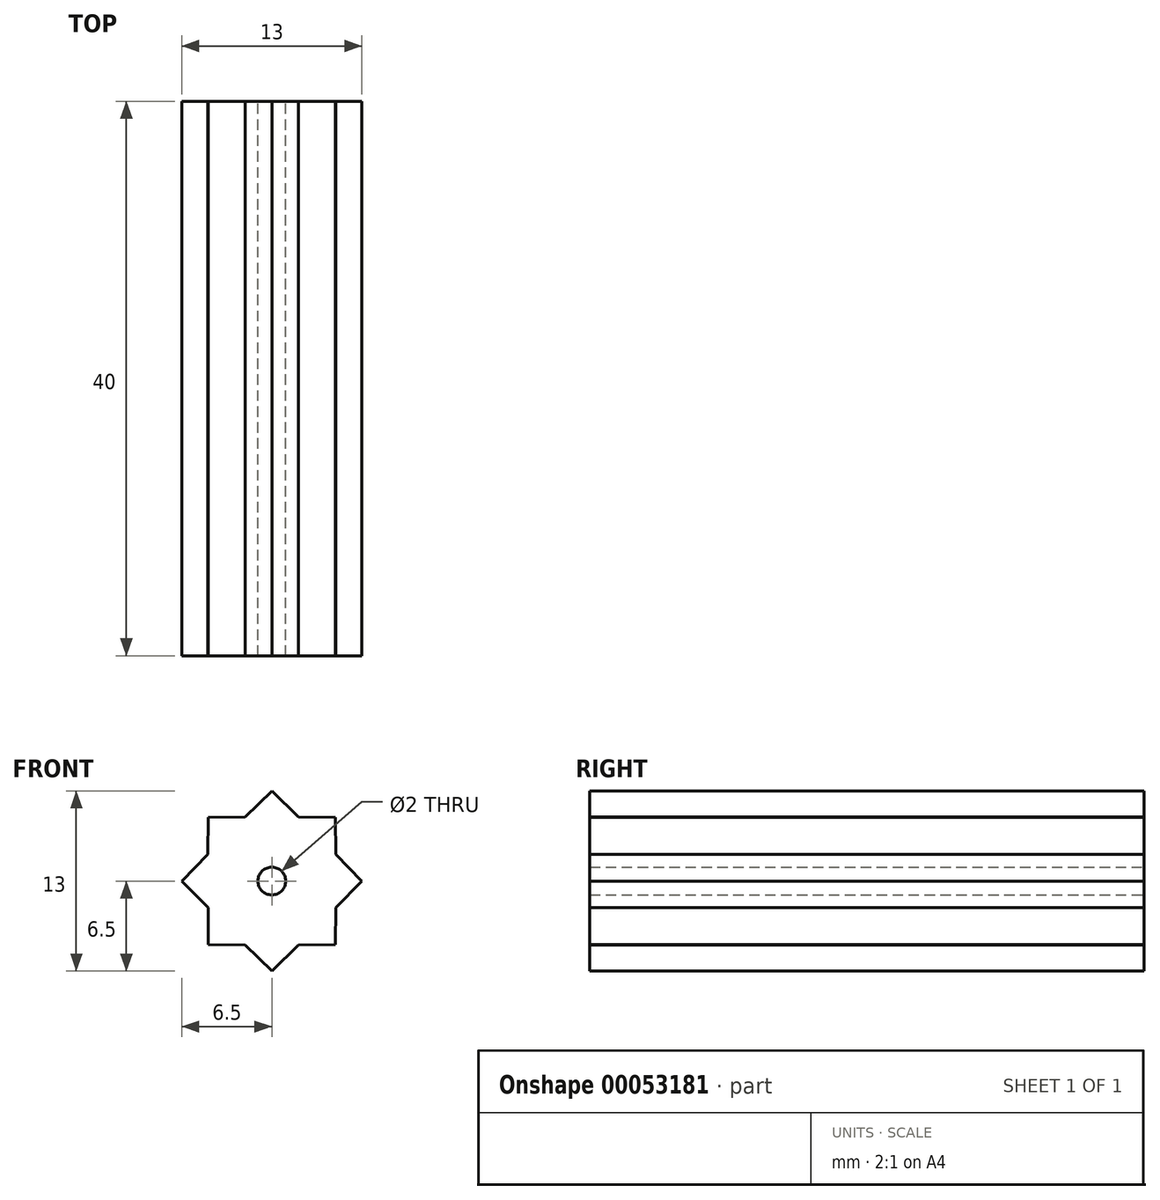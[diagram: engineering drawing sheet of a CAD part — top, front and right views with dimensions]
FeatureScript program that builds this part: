
annotation { "Feature Type Name" : "Feature", "Feature Type Description" : "" }
export const myFeature = defineFeature(function(context is Context, id is Id, definition is map)
    precondition{}
    {
        {
            var Q0;
            Q0=qCreatedBy(makeId("Front.planeOp"),FACE);
            var sketch = newSketch(context, id + "F0", { "sketchPlane" : qUnion([Q0])});
            skCircle(sketch, "E0", {"center": v(0, 0) * mm, "radius": 1 * mm});
            skCircle(sketch, "E1", {"center": v(0, 0) * mm, "radius": 6.5 * mm});
            skPoint(sketch, "E2", {"position": v(-4.6, 4.6) * mm});
            skPoint(sketch, "E3", {"position": v(4.6, 4.6) * mm});
            skPoint(sketch, "E4", {"position": v(4.6, -4.6) * mm});
            skPoint(sketch, "E5", {"position": v(-4.6, -4.6) * mm});
            skLineSegment(sketch, "E6", {"start": v(-1.9, -4.6) * mm, "end": v(-4.6, -4.6) * mm});
            skLineSegment(sketch, "E7", {"start": v(-1.9, -4.6) * mm, "end": v(0, -6.5) * mm});
            skLineSegment(sketch, "E8", {"start": v(-4.6, -4.6) * mm, "end": v(-4.6, -1.9) * mm});
            skLineSegment(sketch, "E9", {"start": v(-4.6, -1.9) * mm, "end": v(-6.5, 0) * mm});
            skLineSegment(sketch, "E10", {"start": v(-6.5, 0) * mm, "end": v(-4.63, 1.92) * mm});
            skLineSegment(sketch, "E11", {"start": v(-4.63, 1.92) * mm, "end": v(-4.6, 4.6) * mm});
            skLineSegment(sketch, "E12", {"start": v(-4.6, 4.6) * mm, "end": v(-1.92, 4.64) * mm});
            skLineSegment(sketch, "E13", {"start": v(-1.92, 4.64) * mm, "end": v(0, 6.5) * mm});
            skLineSegment(sketch, "E14", {"start": v(0, 6.5) * mm, "end": v(1.92, 4.64) * mm});
            skLineSegment(sketch, "E15", {"start": v(1.92, 4.64) * mm, "end": v(4.6, 4.6) * mm});
            skLineSegment(sketch, "E16", {"start": v(4.6, 4.6) * mm, "end": v(4.62, 1.92) * mm});
            skLineSegment(sketch, "E17", {"start": v(4.62, 1.92) * mm, "end": v(6.5, 0) * mm});
            skLineSegment(sketch, "E18", {"start": v(6.5, 0) * mm, "end": v(4.6, -1.9) * mm});
            skLineSegment(sketch, "E19", {"start": v(4.6, -1.9) * mm, "end": v(4.6, -4.6) * mm});
            skLineSegment(sketch, "E20", {"start": v(0, -6.5) * mm, "end": v(1.9, -4.6) * mm});
            skLineSegment(sketch, "E21", {"start": v(1.9, -4.6) * mm, "end": v(4.6, -4.6) * mm});
            skSolve(sketch);
        }
        {
            var Q0;
            Q0=makeQuery(id+"F0.imprint","IMPRINT",FACE,{"disambiguationData":[TD([[makeQuery(id+"F0.imprint","IMPRINT",EDGE,{"derivedFrom":sQuery(id+"F0.wireOp",EDGE,"E0")}),-1.0]])]});
            extrude(context, id + "F1", {"entities" : qUnion([Q0]), "depth" : 40 * mm});
        }
    });
